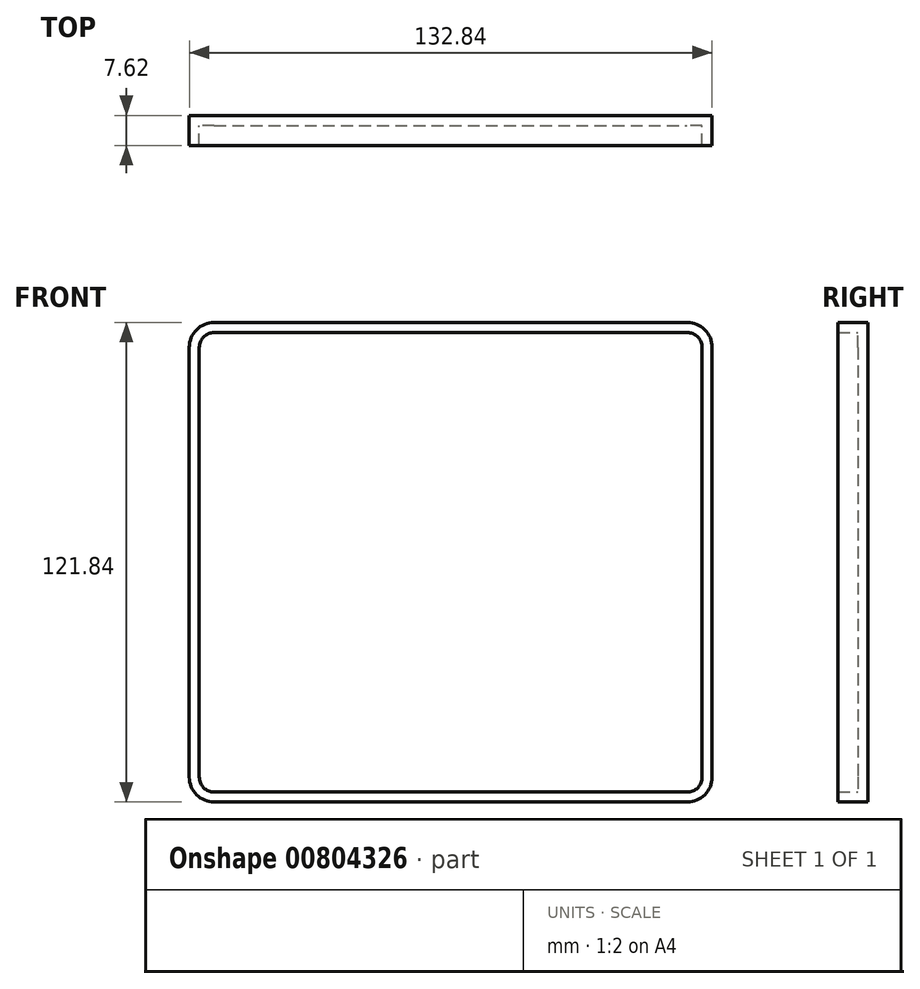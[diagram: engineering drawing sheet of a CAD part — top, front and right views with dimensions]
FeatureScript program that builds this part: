
annotation { "Feature Type Name" : "Feature", "Feature Type Description" : "" }
export const myFeature = defineFeature(function(context is Context, id is Id, definition is map)
    precondition{}
    {
        {
            var Q0;
            Q0=qCreatedBy(makeId("Front.planeOp"),FACE);
            var sketch = newSketch(context, id + "F0", { "sketchPlane" : qUnion([Q0])});
            skLineSegment(sketch, "E0.bottom", {"start": v(-60.68, 60.31) * mm, "end": v(59.46, 60.31) * mm});
            skLineSegment(sketch, "E0.top", {"start": v(-60.68, -61.53) * mm, "end": v(59.46, -61.53) * mm});
            skLineSegment(sketch, "E0.left", {"start": v(-67.03, 53.96) * mm, "end": v(-67.03, -55.18) * mm});
            skLineSegment(sketch, "E0.right", {"start": v(65.8, 53.96) * mm, "end": v(65.8, -55.18) * mm});
            skPoint(sketch, "E1.visualSharp", {"position": v(-67.03, 60.31) * mm});
            skArc(sketch, "E1.filletArc", {"start": v(-60.68, 60.31) * mm, "mid": v(-65.17, 58.45) * mm, "end": v(-67.03, 53.96) * mm});
            skPoint(sketch, "E2.visualSharp", {"position": v(65.8, 60.31) * mm});
            skArc(sketch, "E2.filletArc", {"start": v(65.8, 53.96) * mm, "mid": v(63.95, 58.45) * mm, "end": v(59.46, 60.31) * mm});
            skPoint(sketch, "E3.visualSharp", {"position": v(65.8, -61.53) * mm});
            skArc(sketch, "E3.filletArc", {"start": v(59.46, -61.53) * mm, "mid": v(63.95, -59.67) * mm, "end": v(65.8, -55.18) * mm});
            skPoint(sketch, "E4.visualSharp", {"position": v(-67.03, -61.53) * mm});
            skArc(sketch, "E4.filletArc", {"start": v(-67.03, -55.18) * mm, "mid": v(-65.17, -59.67) * mm, "end": v(-60.68, -61.53) * mm});
            skSolve(sketch);
        }
        {
            var Q0;
            Q0=makeQuery(id+"F0.imprint","IMPRINT",FACE,{"disambiguationData":[TD([[makeQuery(id+"F0.imprint","IMPRINT",EDGE,{"derivedFrom":sQuery(id+"F0.wireOp",EDGE,"E0.bottom")}),-1.0]])]});
            extrude(context, id + "F1", {"entities" : qUnion([Q0]), "depth" : 7.62 * mm, "offsetDistance" : 25.4 * mm});
        }
        {
            var Q0;
            Q0=makeQuery(id+"F1.opExtrude","CAP_FACE",FACE,{"disambiguationData":[OSD([sQuery(id+"F0.wireOp",EDGE,"E0.bottom"),sQuery(id+"F0.wireOp",EDGE,"E0.top"),sQuery(id+"F0.wireOp",EDGE,"E0.left"),sQuery(id+"F0.wireOp",EDGE,"E0.right"),sQuery(id+"F0.wireOp",EDGE,"E1.filletArc"),sQuery(id+"F0.wireOp",EDGE,"E2.filletArc"),sQuery(id+"F0.wireOp",EDGE,"E3.filletArc"),sQuery(id+"F0.wireOp",EDGE,"E4.filletArc")])],"isStart":false});
            shell(context, id + "F2", {"entities" : qUnion([Q0]), "thickness" : 2.54 * mm});
        }
    });
